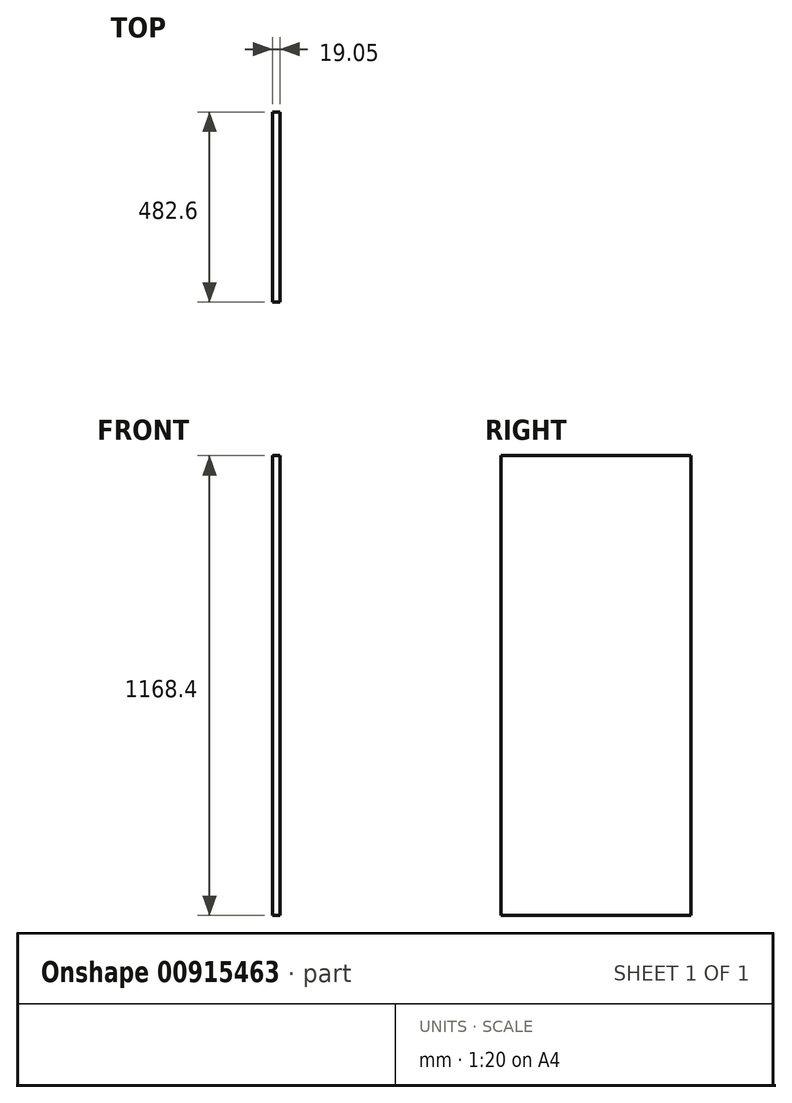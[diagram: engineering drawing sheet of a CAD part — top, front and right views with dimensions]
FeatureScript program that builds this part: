
annotation { "Feature Type Name" : "Feature", "Feature Type Description" : "" }
export const myFeature = defineFeature(function(context is Context, id is Id, definition is map)
    precondition{}
    {
        {
            var Q0;
            Q0=qCreatedBy(makeId("Right.planeOp"),FACE);
            var sketch = newSketch(context, id + "F0", { "sketchPlane" : qUnion([Q0])});
            skLineSegment(sketch, "E0.bottom", {"start": v(241.3, 584.2) * mm, "end": v(-241.3, 584.2) * mm});
            skLineSegment(sketch, "E0.top", {"start": v(241.3, -584.2) * mm, "end": v(-241.3, -584.2) * mm});
            skLineSegment(sketch, "E0.left", {"start": v(241.3, 584.2) * mm, "end": v(241.3, -584.2) * mm});
            skLineSegment(sketch, "E0.right", {"start": v(-241.3, 584.2) * mm, "end": v(-241.3, -584.2) * mm});
            skPoint(sketch, "E0.middle", {"position": v(0, 0) * mm});
            skSolve(sketch);
        }
        {
            var Q0;
            Q0=makeQuery(id+"F0.imprint","IMPRINT",FACE,{"disambiguationData":[TD([[makeQuery(id+"F0.imprint","IMPRINT",EDGE,{"derivedFrom":sQuery(id+"F0.wireOp",EDGE,"E0.bottom")}),1.0]])]});
            extrude(context, id + "F1", {"entities" : qUnion([Q0]), "depth" : 19.05 * mm, "offsetDistance" : 25.4 * mm});
        }
    });
